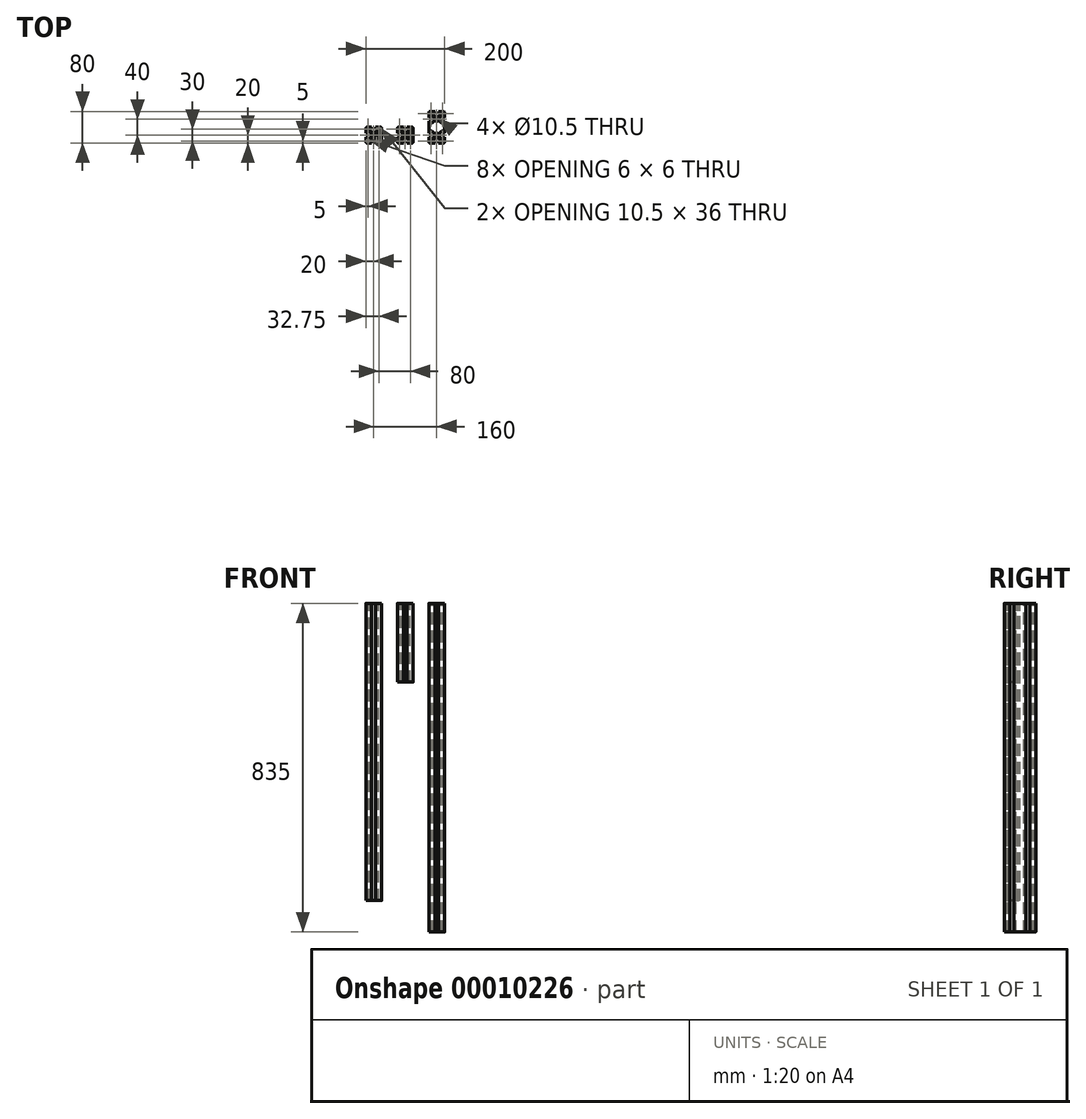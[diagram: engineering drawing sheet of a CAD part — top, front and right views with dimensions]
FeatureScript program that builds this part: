
annotation { "Feature Type Name" : "Feature", "Feature Type Description" : "" }
export const myFeature = defineFeature(function(context is Context, id is Id, definition is map)
    precondition{}
    {
        {
            var Q0;
            Q0=qCreatedBy(makeId("Top.planeOp"),FACE);
            var sketch = newSketch(context, id + "F0", { "sketchPlane" : qUnion([Q0])});
            skLineSegment(sketch, "E0.bottom", {"start": v(97, 20) * mm, "end": v(63, 20) * mm});
            skLineSegment(sketch, "E0.top", {"start": v(97, -20) * mm, "end": v(63, -20) * mm});
            skLineSegment(sketch, "E0.left", {"start": v(100, 17) * mm, "end": v(100, -17) * mm});
            skLineSegment(sketch, "E0.right", {"start": v(60, 17) * mm, "end": v(60, -17) * mm});
            skPoint(sketch, "E1", {"position": v(80, -20) * mm});
            skPoint(sketch, "E2", {"position": v(100, 0) * mm});
            skCircle(sketch, "E3", {"center": v(80, 0) * mm, "radius": 5.25 * mm});
            skPoint(sketch, "E4.visualSharp", {"position": v(100, 20) * mm});
            skArc(sketch, "E4.filletArc", {"start": v(100, 17) * mm, "mid": v(99.12, 19.12) * mm, "end": v(97, 20) * mm});
            skPoint(sketch, "E5.visualSharp", {"position": v(60, 20) * mm});
            skArc(sketch, "E5.filletArc", {"start": v(63, 20) * mm, "mid": v(60.88, 19.12) * mm, "end": v(60, 17) * mm});
            skPoint(sketch, "E6.visualSharp", {"position": v(60, -20) * mm});
            skArc(sketch, "E6.filletArc", {"start": v(60, -17) * mm, "mid": v(60.88, -19.12) * mm, "end": v(63, -20) * mm});
            skPoint(sketch, "E7.visualSharp", {"position": v(100, -20) * mm});
            skArc(sketch, "E7.filletArc", {"start": v(97, -20) * mm, "mid": v(99.12, -19.12) * mm, "end": v(100, -17) * mm});
            skLineSegment(sketch, "E8", {"start": v(85, 20) * mm, "end": v(85, 14.5) * mm});
            skLineSegment(sketch, "E9", {"start": v(85, 14.5) * mm, "end": v(90, 14.5) * mm});
            skLineSegment(sketch, "E10", {"start": v(90, 14.5) * mm, "end": v(90, 12.5) * mm});
            skLineSegment(sketch, "E11", {"start": v(90, 12.5) * mm, "end": v(85, 7.5) * mm});
            skLineSegment(sketch, "E12", {"start": v(85, 7.5) * mm, "end": v(75, 7.5) * mm});
            skLineSegment(sketch, "E13", {"start": v(75, 7.5) * mm, "end": v(70, 12.5) * mm});
            skLineSegment(sketch, "E14", {"start": v(70, 12.5) * mm, "end": v(70, 14.5) * mm});
            skLineSegment(sketch, "E15", {"start": v(70, 14.5) * mm, "end": v(75, 14.5) * mm});
            skLineSegment(sketch, "E16", {"start": v(75, 14.5) * mm, "end": v(75, 20) * mm});
            skPoint(sketch, "E17", {"position": v(80, 7.5) * mm});
            skLineSegment(sketch, "E18.bottom", {"start": v(67, 12) * mm, "end": v(63, 12) * mm});
            skLineSegment(sketch, "E18.top", {"start": v(67, 18) * mm, "end": v(63, 18) * mm});
            skLineSegment(sketch, "E18.left", {"start": v(68, 13) * mm, "end": v(68, 17) * mm});
            skLineSegment(sketch, "E18.right", {"start": v(62, 13) * mm, "end": v(62, 17) * mm});
            skPoint(sketch, "E19.visualSharp", {"position": v(62, 18) * mm});
            skArc(sketch, "E19.filletArc", {"start": v(63, 18) * mm, "mid": v(62.3, 17.7) * mm, "end": v(62, 17) * mm});
            skPoint(sketch, "E20.visualSharp", {"position": v(62, 12) * mm});
            skArc(sketch, "E20.filletArc", {"start": v(62, 13) * mm, "mid": v(62.3, 12.3) * mm, "end": v(63, 12) * mm});
            skPoint(sketch, "E21.visualSharp", {"position": v(68, 12) * mm});
            skArc(sketch, "E21.filletArc", {"start": v(67, 12) * mm, "mid": v(67.7, 12.3) * mm, "end": v(68, 13) * mm});
            skPoint(sketch, "E22.visualSharp", {"position": v(68, 18) * mm});
            skArc(sketch, "E22.filletArc", {"start": v(68, 17) * mm, "mid": v(67.7, 17.7) * mm, "end": v(67, 18) * mm});
            skLineSegment(sketch, "E23.1.0", {"start": v(60, 5) * mm, "end": v(65.5, 5) * mm});
            skLineSegment(sketch, "E23.1.1", {"start": v(65.5, 5) * mm, "end": v(65.5, 10) * mm});
            skLineSegment(sketch, "E23.1.2", {"start": v(65.5, 10) * mm, "end": v(67.5, 10) * mm});
            skLineSegment(sketch, "E23.1.3", {"start": v(67.5, 10) * mm, "end": v(72.5, 5) * mm});
            skLineSegment(sketch, "E23.1.4", {"start": v(72.5, 5) * mm, "end": v(72.5, -5) * mm});
            skLineSegment(sketch, "E23.1.5", {"start": v(72.5, -5) * mm, "end": v(67.5, -10) * mm});
            skLineSegment(sketch, "E23.1.6", {"start": v(67.5, -10) * mm, "end": v(65.5, -10) * mm});
            skLineSegment(sketch, "E23.1.7", {"start": v(65.5, -10) * mm, "end": v(65.5, -5) * mm});
            skLineSegment(sketch, "E23.1.8", {"start": v(65.5, -5) * mm, "end": v(60, -5) * mm});
            skLineSegment(sketch, "E23.1.9", {"start": v(67, -12) * mm, "end": v(63, -12) * mm});
            skArc(sketch, "E23.1.10", {"start": v(63, -12) * mm, "mid": v(62.3, -12.3) * mm, "end": v(62, -13) * mm});
            skLineSegment(sketch, "E23.1.11", {"start": v(62, -13) * mm, "end": v(62, -17) * mm});
            skArc(sketch, "E23.1.12", {"start": v(62, -17) * mm, "mid": v(62.3, -17.7) * mm, "end": v(63, -18) * mm});
            skLineSegment(sketch, "E23.1.13", {"start": v(67, -18) * mm, "end": v(63, -18) * mm});
            skArc(sketch, "E23.1.14", {"start": v(67, -18) * mm, "mid": v(67.7, -17.7) * mm, "end": v(68, -17) * mm});
            skLineSegment(sketch, "E23.1.15", {"start": v(68, -13) * mm, "end": v(68, -17) * mm});
            skArc(sketch, "E23.1.16", {"start": v(68, -13) * mm, "mid": v(67.7, -12.3) * mm, "end": v(67, -12) * mm});
            skLineSegment(sketch, "E23.2.0", {"start": v(75, -20) * mm, "end": v(75, -14.5) * mm});
            skLineSegment(sketch, "E23.2.1", {"start": v(75, -14.5) * mm, "end": v(70, -14.5) * mm});
            skLineSegment(sketch, "E23.2.2", {"start": v(70, -14.5) * mm, "end": v(70, -12.5) * mm});
            skLineSegment(sketch, "E23.2.3", {"start": v(70, -12.5) * mm, "end": v(75, -7.5) * mm});
            skLineSegment(sketch, "E23.2.4", {"start": v(75, -7.5) * mm, "end": v(85, -7.5) * mm});
            skLineSegment(sketch, "E23.2.5", {"start": v(85, -7.5) * mm, "end": v(90, -12.5) * mm});
            skLineSegment(sketch, "E23.2.6", {"start": v(90, -12.5) * mm, "end": v(90, -14.5) * mm});
            skLineSegment(sketch, "E23.2.7", {"start": v(90, -14.5) * mm, "end": v(85, -14.5) * mm});
            skLineSegment(sketch, "E23.2.8", {"start": v(85, -14.5) * mm, "end": v(85, -20) * mm});
            skArc(sketch, "E24.1", {"start": v(97, -18) * mm, "mid": v(97.7, -17.7) * mm, "end": v(98, -17) * mm});
            skArc(sketch, "E24.5", {"start": v(98, 17) * mm, "mid": v(97.7, 17.7) * mm, "end": v(97, 18) * mm});
            skLineSegment(sketch, "E25", {"start": v(97, -18) * mm, "end": v(93, -18) * mm});
            skLineSegment(sketch, "E26", {"start": v(92, -17) * mm, "end": v(92, -9.5) * mm});
            skLineSegment(sketch, "E27", {"start": v(92, -9.5) * mm, "end": v(87.5, -5) * mm});
            skLineSegment(sketch, "E28", {"start": v(87.5, -5) * mm, "end": v(87.5, 5) * mm});
            skLineSegment(sketch, "E29", {"start": v(87.5, 5) * mm, "end": v(92, 9.5) * mm});
            skLineSegment(sketch, "E30", {"start": v(92, 9.5) * mm, "end": v(92, 17) * mm});
            skLineSegment(sketch, "E31", {"start": v(93, 18) * mm, "end": v(97, 18) * mm});
            skPoint(sketch, "E32", {"position": v(87.5, 0) * mm});
            skPoint(sketch, "E33.visualSharp", {"position": v(92, -18) * mm});
            skArc(sketch, "E33.filletArc", {"start": v(92, -17) * mm, "mid": v(92.3, -17.7) * mm, "end": v(93, -18) * mm});
            skPoint(sketch, "E34.visualSharp", {"position": v(92, 18) * mm});
            skArc(sketch, "E34.filletArc", {"start": v(93, 18) * mm, "mid": v(92.3, 17.7) * mm, "end": v(92, 17) * mm});
            skLineSegment(sketch, "E35", {"start": v(98, -17) * mm, "end": v(98, 17) * mm});
            skSolve(sketch);
        }
        {
            var Q0;
            Q0=makeQuery(id+"F0.imprint","IMPRINT",FACE,{"disambiguationData":[TD([[makeQuery(id+"F0.imprint","IMPRINT",EDGE,{"derivedFrom":sQuery(id+"F0.wireOp",EDGE,"E0.left")}),-1.0]])]});
            extrude(context, id + "F1", {"entities" : qUnion([Q0]), "oppositeDirection" : true, "depth" : 755 * mm});
        }
        {
            var Q0;
            Q0=makeQuery(id+"F1.opExtrude","SWEPT_BODY",BODY,{"disambiguationData":[OSD([sQuery(id+"F0.wireOp",EDGE,"E0.bottom"),sQuery(id+"F0.wireOp",EDGE,"E0.top"),sQuery(id+"F0.wireOp",EDGE,"E0.left"),sQuery(id+"F0.wireOp",EDGE,"E0.right"),sQuery(id+"F0.wireOp",EDGE,"E3"),sQuery(id+"F0.wireOp",EDGE,"E4.filletArc"),sQuery(id+"F0.wireOp",EDGE,"E5.filletArc"),sQuery(id+"F0.wireOp",EDGE,"E6.filletArc"),sQuery(id+"F0.wireOp",EDGE,"E7.filletArc"),sQuery(id+"F0.wireOp",EDGE,"E8"),sQuery(id+"F0.wireOp",EDGE,"E9"),sQuery(id+"F0.wireOp",EDGE,"E10"),sQuery(id+"F0.wireOp",EDGE,"E11"),sQuery(id+"F0.wireOp",EDGE,"E12"),sQuery(id+"F0.wireOp",EDGE,"E13"),sQuery(id+"F0.wireOp",EDGE,"E14"),sQuery(id+"F0.wireOp",EDGE,"E15"),sQuery(id+"F0.wireOp",EDGE,"E16"),sQuery(id+"F0.wireOp",EDGE,"E18.bottom"),sQuery(id+"F0.wireOp",EDGE,"E18.top"),sQuery(id+"F0.wireOp",EDGE,"E18.left"),sQuery(id+"F0.wireOp",EDGE,"E18.right"),sQuery(id+"F0.wireOp",EDGE,"E19.filletArc"),sQuery(id+"F0.wireOp",EDGE,"E20.filletArc"),sQuery(id+"F0.wireOp",EDGE,"E21.filletArc"),sQuery(id+"F0.wireOp",EDGE,"E22.filletArc"),sQuery(id+"F0.wireOp",EDGE,"E23.1.0"),sQuery(id+"F0.wireOp",EDGE,"E23.1.1"),sQuery(id+"F0.wireOp",EDGE,"E23.1.2"),sQuery(id+"F0.wireOp",EDGE,"E23.1.3"),sQuery(id+"F0.wireOp",EDGE,"E23.1.4"),sQuery(id+"F0.wireOp",EDGE,"E23.1.5"),sQuery(id+"F0.wireOp",EDGE,"E23.1.6"),sQuery(id+"F0.wireOp",EDGE,"E23.1.7"),sQuery(id+"F0.wireOp",EDGE,"E23.1.8"),sQuery(id+"F0.wireOp",EDGE,"E23.1.9"),sQuery(id+"F0.wireOp",EDGE,"E23.1.10"),sQuery(id+"F0.wireOp",EDGE,"E23.1.11"),sQuery(id+"F0.wireOp",EDGE,"E23.1.12"),sQuery(id+"F0.wireOp",EDGE,"E23.1.13"),sQuery(id+"F0.wireOp",EDGE,"E23.1.14"),sQuery(id+"F0.wireOp",EDGE,"E23.1.15"),sQuery(id+"F0.wireOp",EDGE,"E23.1.16"),sQuery(id+"F0.wireOp",EDGE,"E23.2.0"),sQuery(id+"F0.wireOp",EDGE,"E23.2.1"),sQuery(id+"F0.wireOp",EDGE,"E23.2.2"),sQuery(id+"F0.wireOp",EDGE,"E23.2.3"),sQuery(id+"F0.wireOp",EDGE,"E23.2.4"),sQuery(id+"F0.wireOp",EDGE,"E23.2.5"),sQuery(id+"F0.wireOp",EDGE,"E23.2.6"),sQuery(id+"F0.wireOp",EDGE,"E23.2.7"),sQuery(id+"F0.wireOp",EDGE,"E23.2.8"),sQuery(id+"F0.wireOp",EDGE,"E24.1"),sQuery(id+"F0.wireOp",EDGE,"E24.5"),sQuery(id+"F0.wireOp",EDGE,"E25"),sQuery(id+"F0.wireOp",EDGE,"E26"),sQuery(id+"F0.wireOp",EDGE,"E27"),sQuery(id+"F0.wireOp",EDGE,"E28"),sQuery(id+"F0.wireOp",EDGE,"E29"),sQuery(id+"F0.wireOp",EDGE,"E30"),sQuery(id+"F0.wireOp",EDGE,"E31"),sQuery(id+"F0.wireOp",EDGE,"E33.filletArc"),sQuery(id+"F0.wireOp",EDGE,"E34.filletArc"),sQuery(id+"F0.wireOp",EDGE,"E35")])]});
            transform(context, id + "F2", {"entities" : qUnion([Q0]), "transformType" : TransformType.TRANSLATION_3D, "dx" : 80 * mm, "dy" : 0 * mm, "dz" : 0 * mm, "makeCopy" : true});
        }
        {
            var Q0;
            Q0=makeQuery(id+"F2.opPattern","COPY",FACE,{"derivedFrom":makeQuery(id+"F1.opExtrude","CAP_FACE",FACE,{"disambiguationData":[OSD([sQuery(id+"F0.wireOp",EDGE,"E0.bottom"),sQuery(id+"F0.wireOp",EDGE,"E0.top"),sQuery(id+"F0.wireOp",EDGE,"E0.left"),sQuery(id+"F0.wireOp",EDGE,"E0.right"),sQuery(id+"F0.wireOp",EDGE,"E3"),sQuery(id+"F0.wireOp",EDGE,"E4.filletArc"),sQuery(id+"F0.wireOp",EDGE,"E5.filletArc"),sQuery(id+"F0.wireOp",EDGE,"E6.filletArc"),sQuery(id+"F0.wireOp",EDGE,"E7.filletArc"),sQuery(id+"F0.wireOp",EDGE,"E8"),sQuery(id+"F0.wireOp",EDGE,"E9"),sQuery(id+"F0.wireOp",EDGE,"E10"),sQuery(id+"F0.wireOp",EDGE,"E11"),sQuery(id+"F0.wireOp",EDGE,"E12"),sQuery(id+"F0.wireOp",EDGE,"E13"),sQuery(id+"F0.wireOp",EDGE,"E14"),sQuery(id+"F0.wireOp",EDGE,"E15"),sQuery(id+"F0.wireOp",EDGE,"E16"),sQuery(id+"F0.wireOp",EDGE,"E18.bottom"),sQuery(id+"F0.wireOp",EDGE,"E18.top"),sQuery(id+"F0.wireOp",EDGE,"E18.left"),sQuery(id+"F0.wireOp",EDGE,"E18.right"),sQuery(id+"F0.wireOp",EDGE,"E19.filletArc"),sQuery(id+"F0.wireOp",EDGE,"E20.filletArc"),sQuery(id+"F0.wireOp",EDGE,"E21.filletArc"),sQuery(id+"F0.wireOp",EDGE,"E22.filletArc"),sQuery(id+"F0.wireOp",EDGE,"E23.1.0"),sQuery(id+"F0.wireOp",EDGE,"E23.1.1"),sQuery(id+"F0.wireOp",EDGE,"E23.1.2"),sQuery(id+"F0.wireOp",EDGE,"E23.1.3"),sQuery(id+"F0.wireOp",EDGE,"E23.1.4"),sQuery(id+"F0.wireOp",EDGE,"E23.1.5"),sQuery(id+"F0.wireOp",EDGE,"E23.1.6"),sQuery(id+"F0.wireOp",EDGE,"E23.1.7"),sQuery(id+"F0.wireOp",EDGE,"E23.1.8"),sQuery(id+"F0.wireOp",EDGE,"E23.1.9"),sQuery(id+"F0.wireOp",EDGE,"E23.1.10"),sQuery(id+"F0.wireOp",EDGE,"E23.1.11"),sQuery(id+"F0.wireOp",EDGE,"E23.1.12"),sQuery(id+"F0.wireOp",EDGE,"E23.1.13"),sQuery(id+"F0.wireOp",EDGE,"E23.1.14"),sQuery(id+"F0.wireOp",EDGE,"E23.1.15"),sQuery(id+"F0.wireOp",EDGE,"E23.1.16"),sQuery(id+"F0.wireOp",EDGE,"E23.2.0"),sQuery(id+"F0.wireOp",EDGE,"E23.2.1"),sQuery(id+"F0.wireOp",EDGE,"E23.2.2"),sQuery(id+"F0.wireOp",EDGE,"E23.2.3"),sQuery(id+"F0.wireOp",EDGE,"E23.2.4"),sQuery(id+"F0.wireOp",EDGE,"E23.2.5"),sQuery(id+"F0.wireOp",EDGE,"E23.2.6"),sQuery(id+"F0.wireOp",EDGE,"E23.2.7"),sQuery(id+"F0.wireOp",EDGE,"E23.2.8"),sQuery(id+"F0.wireOp",EDGE,"E24.1"),sQuery(id+"F0.wireOp",EDGE,"E24.5"),sQuery(id+"F0.wireOp",EDGE,"E25"),sQuery(id+"F0.wireOp",EDGE,"E26"),sQuery(id+"F0.wireOp",EDGE,"E27"),sQuery(id+"F0.wireOp",EDGE,"E28"),sQuery(id+"F0.wireOp",EDGE,"E29"),sQuery(id+"F0.wireOp",EDGE,"E30"),sQuery(id+"F0.wireOp",EDGE,"E31"),sQuery(id+"F0.wireOp",EDGE,"E33.filletArc"),sQuery(id+"F0.wireOp",EDGE,"E34.filletArc"),sQuery(id+"F0.wireOp",EDGE,"E35")])],"isStart":false}),"instanceName":"1"});
            extrude(context, id + "F3", {"entities" : qUnion([Q0]), "operationType" : NewBodyOperationType.REMOVE, "oppositeDirection" : true, "depth" : 555 * mm});
        }
        {
            var Q0;
            Q0=qCreatedBy(makeId("Top.planeOp"),FACE);
            var sketch = newSketch(context, id + "F4", { "sketchPlane" : qUnion([Q0])});
            skLineSegment(sketch, "E36.top", {"start": v(257, -20) * mm, "end": v(223, -20) * mm});
            skLineSegment(sketch, "E36.left", {"start": v(260, 17) * mm, "end": v(260, -17) * mm});
            skLineSegment(sketch, "E36.right", {"start": v(220, 17) * mm, "end": v(220, -17) * mm});
            skPoint(sketch, "E37", {"position": v(240, -20) * mm});
            skPoint(sketch, "E38", {"position": v(260, 0) * mm});
            skCircle(sketch, "E39", {"center": v(240, 0) * mm, "radius": 5.25 * mm});
            skPoint(sketch, "E40.visualSharp", {"position": v(220, -20) * mm});
            skArc(sketch, "E40.filletArc", {"start": v(220, -17) * mm, "mid": v(220.88, -19.12) * mm, "end": v(223, -20) * mm});
            skPoint(sketch, "E41.visualSharp", {"position": v(260, -20) * mm});
            skArc(sketch, "E41.filletArc", {"start": v(257, -20) * mm, "mid": v(259.12, -19.12) * mm, "end": v(260, -17) * mm});
            skLineSegment(sketch, "E42.1.9", {"start": v(227, -12) * mm, "end": v(223, -12) * mm});
            skArc(sketch, "E42.1.10", {"start": v(223, -12) * mm, "mid": v(222.3, -12.3) * mm, "end": v(222, -13) * mm});
            skLineSegment(sketch, "E42.1.11", {"start": v(222, -13) * mm, "end": v(222, -17) * mm});
            skArc(sketch, "E42.1.12", {"start": v(222, -17) * mm, "mid": v(222.3, -17.7) * mm, "end": v(223, -18) * mm});
            skLineSegment(sketch, "E42.1.13", {"start": v(227, -18) * mm, "end": v(223, -18) * mm});
            skArc(sketch, "E42.1.14", {"start": v(227, -18) * mm, "mid": v(227.7, -17.7) * mm, "end": v(228, -17) * mm});
            skLineSegment(sketch, "E42.1.15", {"start": v(228, -13) * mm, "end": v(228, -17) * mm});
            skArc(sketch, "E42.1.16", {"start": v(228, -13) * mm, "mid": v(227.7, -12.3) * mm, "end": v(227, -12) * mm});
            skLineSegment(sketch, "E42.2.0", {"start": v(235, -20) * mm, "end": v(235, -14.5) * mm});
            skLineSegment(sketch, "E42.2.1", {"start": v(235, -14.5) * mm, "end": v(230, -14.5) * mm});
            skLineSegment(sketch, "E42.2.2", {"start": v(230, -14.5) * mm, "end": v(230, -12.5) * mm});
            skLineSegment(sketch, "E42.2.3", {"start": v(230, -12.5) * mm, "end": v(235, -7.5) * mm});
            skLineSegment(sketch, "E42.2.4", {"start": v(235, -7.5) * mm, "end": v(245, -7.5) * mm});
            skLineSegment(sketch, "E42.2.5", {"start": v(245, -7.5) * mm, "end": v(250, -12.5) * mm});
            skLineSegment(sketch, "E42.2.6", {"start": v(250, -12.5) * mm, "end": v(250, -14.5) * mm});
            skLineSegment(sketch, "E42.2.7", {"start": v(250, -14.5) * mm, "end": v(245, -14.5) * mm});
            skLineSegment(sketch, "E42.2.8", {"start": v(245, -14.5) * mm, "end": v(245, -20) * mm});
            skLineSegment(sketch, "E43.1.0", {"start": v(247.5, 5) * mm, "end": v(252.5, 10) * mm});
            skLineSegment(sketch, "E43.1.2", {"start": v(253, -18) * mm, "end": v(257, -18) * mm});
            skLineSegment(sketch, "E43.1.3", {"start": v(252.5, -10) * mm, "end": v(247.5, -5) * mm});
            skLineSegment(sketch, "E43.1.4", {"start": v(258, -13) * mm, "end": v(258, -17) * mm});
            skLineSegment(sketch, "E43.1.5", {"start": v(252, -13) * mm, "end": v(252, -17) * mm});
            skLineSegment(sketch, "E43.1.6", {"start": v(254.5, -5) * mm, "end": v(254.5, -10) * mm});
            skLineSegment(sketch, "E43.1.7", {"start": v(260, -5) * mm, "end": v(254.5, -5) * mm});
            skLineSegment(sketch, "E43.1.8", {"start": v(247.5, -5) * mm, "end": v(247.5, 5) * mm});
            skLineSegment(sketch, "E43.1.9", {"start": v(254.5, 5) * mm, "end": v(260, 5) * mm});
            skLineSegment(sketch, "E43.1.10", {"start": v(253, -12) * mm, "end": v(257, -12) * mm});
            skLineSegment(sketch, "E43.1.11", {"start": v(254.5, 10) * mm, "end": v(254.5, 5) * mm});
            skLineSegment(sketch, "E43.1.13", {"start": v(254.5, -10) * mm, "end": v(252.5, -10) * mm});
            skArc(sketch, "E43.1.14", {"start": v(252, -17) * mm, "mid": v(252.3, -17.7) * mm, "end": v(253, -18) * mm});
            skLineSegment(sketch, "E43.1.15", {"start": v(252.5, 10) * mm, "end": v(254.5, 10) * mm});
            skArc(sketch, "E43.1.16", {"start": v(257, -18) * mm, "mid": v(257.7, -17.7) * mm, "end": v(258, -17) * mm});
            skArc(sketch, "E43.1.17", {"start": v(258, -13) * mm, "mid": v(257.7, -12.3) * mm, "end": v(257, -12) * mm});
            skArc(sketch, "E43.1.18", {"start": v(253, -12) * mm, "mid": v(252.3, -12.3) * mm, "end": v(252, -13) * mm});
            skLineSegment(sketch, "E43.3.0", {"start": v(232.5, -5) * mm, "end": v(227.5, -10) * mm});
            skPoint(sketch, "E43.3.1", {"position": v(220, 0) * mm});
            skLineSegment(sketch, "E43.3.3", {"start": v(227.5, 10) * mm, "end": v(232.5, 5) * mm});
            skLineSegment(sketch, "E43.3.6", {"start": v(225.5, 5) * mm, "end": v(225.5, 10) * mm});
            skLineSegment(sketch, "E43.3.7", {"start": v(220, 5) * mm, "end": v(225.5, 5) * mm});
            skLineSegment(sketch, "E43.3.8", {"start": v(232.5, 5) * mm, "end": v(232.5, -5) * mm});
            skLineSegment(sketch, "E43.3.9", {"start": v(225.5, -5) * mm, "end": v(220, -5) * mm});
            skLineSegment(sketch, "E43.3.11", {"start": v(225.5, -10) * mm, "end": v(225.5, -5) * mm});
            skLineSegment(sketch, "E43.3.13", {"start": v(225.5, 10) * mm, "end": v(227.5, 10) * mm});
            skLineSegment(sketch, "E43.3.15", {"start": v(227.5, -10) * mm, "end": v(225.5, -10) * mm});
            skPoint(sketch, "E44.0.MirrorP", {"position": v(240, 40) * mm});
            skPoint(sketch, "E44.1.MirrorP", {"position": v(240, 40) * mm});
            skPoint(sketch, "E44.4.MirrorP", {"position": v(240, 40) * mm});
            skArc(sketch, "E44.5.MirrorCS", {"start": v(222, 57) * mm, "mid": v(222.3, 57.7) * mm, "end": v(223, 58) * mm});
            skArc(sketch, "E44.6.MirrorCS", {"start": v(257, 58) * mm, "mid": v(257.7, 57.7) * mm, "end": v(258, 57) * mm});
            skLineSegment(sketch, "E44.8.MirrorCS", {"start": v(227.5, 50) * mm, "end": v(225.5, 50) * mm});
            skLineSegment(sketch, "E44.9.MirrorCS", {"start": v(250, 52.5) * mm, "end": v(250, 54.5) * mm});
            skPoint(sketch, "E44.10.MirrorP", {"position": v(240, 40) * mm});
            skLineSegment(sketch, "E44.12.MirrorCS", {"start": v(252.5, 30) * mm, "end": v(254.5, 30) * mm});
            skArc(sketch, "E44.13.MirrorCS", {"start": v(253, 52) * mm, "mid": v(252.3, 52.3) * mm, "end": v(252, 53) * mm});
            skLineSegment(sketch, "E44.15.MirrorCS", {"start": v(254.5, 50) * mm, "end": v(252.5, 50) * mm});
            skLineSegment(sketch, "E44.16.MirrorCS", {"start": v(225.5, 30) * mm, "end": v(227.5, 30) * mm});
            skArc(sketch, "E44.17.MirrorCS", {"start": v(257, 60) * mm, "mid": v(259.12, 59.12) * mm, "end": v(260, 57) * mm});
            skLineSegment(sketch, "E44.19.MirrorCS", {"start": v(230, 54.5) * mm, "end": v(230, 52.5) * mm});
            skArc(sketch, "E44.20.MirrorCS", {"start": v(220, 57) * mm, "mid": v(220.88, 59.12) * mm, "end": v(223, 60) * mm});
            skArc(sketch, "E44.23.MirrorCS", {"start": v(228, 53) * mm, "mid": v(227.7, 52.3) * mm, "end": v(227, 52) * mm});
            skArc(sketch, "E44.24.MirrorCS", {"start": v(223, 52) * mm, "mid": v(222.3, 52.3) * mm, "end": v(222, 53) * mm});
            skArc(sketch, "E44.25.MirrorCS", {"start": v(258, 53) * mm, "mid": v(257.7, 52.3) * mm, "end": v(257, 52) * mm});
            skArc(sketch, "E44.29.MirrorCS", {"start": v(252, 57) * mm, "mid": v(252.3, 57.7) * mm, "end": v(253, 58) * mm});
            skArc(sketch, "E44.31.MirrorCS", {"start": v(227, 58) * mm, "mid": v(227.7, 57.7) * mm, "end": v(228, 57) * mm});
            skLineSegment(sketch, "E44.32.MirrorCS", {"start": v(225.5, 35) * mm, "end": v(225.5, 30) * mm});
            skLineSegment(sketch, "E44.34.MirrorCS", {"start": v(247.5, 45) * mm, "end": v(247.5, 35) * mm});
            skLineSegment(sketch, "E44.35.MirrorCS", {"start": v(235, 60) * mm, "end": v(235, 54.5) * mm});
            skLineSegment(sketch, "E44.38.MirrorCS", {"start": v(258, 53) * mm, "end": v(258, 57) * mm});
            skPoint(sketch, "E44.39.MirrorP", {"position": v(260, 60) * mm});
            skLineSegment(sketch, "E44.40.MirrorCS", {"start": v(260, 45) * mm, "end": v(254.5, 45) * mm});
            skLineSegment(sketch, "E44.41.MirrorCS", {"start": v(247.5, 35) * mm, "end": v(252.5, 30) * mm});
            skLineSegment(sketch, "E44.42.MirrorCS", {"start": v(254.5, 45) * mm, "end": v(254.5, 50) * mm});
            skLineSegment(sketch, "E44.43.MirrorCS", {"start": v(225.5, 45) * mm, "end": v(220, 45) * mm});
            skLineSegment(sketch, "E44.44.MirrorCS", {"start": v(254.5, 30) * mm, "end": v(254.5, 35) * mm});
            skLineSegment(sketch, "E44.46.MirrorCS", {"start": v(230, 52.5) * mm, "end": v(235, 47.5) * mm});
            skLineSegment(sketch, "E44.47.MirrorCS", {"start": v(245, 47.5) * mm, "end": v(250, 52.5) * mm});
            skLineSegment(sketch, "E44.48.MirrorCS", {"start": v(227.5, 30) * mm, "end": v(232.5, 35) * mm});
            skLineSegment(sketch, "E44.49.MirrorCS", {"start": v(232.5, 35) * mm, "end": v(232.5, 45) * mm});
            skPoint(sketch, "E44.50.MirrorP", {"position": v(220, 20) * mm});
            skPoint(sketch, "E44.51.MirrorP", {"position": v(220, 40) * mm});
            skLineSegment(sketch, "E44.52.MirrorCS", {"start": v(250, 54.5) * mm, "end": v(245, 54.5) * mm});
            skCircle(sketch, "E44.53.MirrorC", {"center": v(240, 40) * mm, "radius": 5.25 * mm});
            skLineSegment(sketch, "E44.57.MirrorCS", {"start": v(254.5, 35) * mm, "end": v(260, 35) * mm});
            skPoint(sketch, "E44.58.MirrorP", {"position": v(240, 40) * mm});
            skLineSegment(sketch, "E44.60.MirrorCS", {"start": v(225.5, 50) * mm, "end": v(225.5, 45) * mm});
            skLineSegment(sketch, "E44.61.MirrorCS", {"start": v(235, 47.5) * mm, "end": v(245, 47.5) * mm});
            skLineSegment(sketch, "E44.62.MirrorCS", {"start": v(227, 52) * mm, "end": v(223, 52) * mm});
            skLineSegment(sketch, "E44.63.MirrorCS", {"start": v(253, 58) * mm, "end": v(257, 58) * mm});
            skLineSegment(sketch, "E44.64.MirrorCS", {"start": v(227, 58) * mm, "end": v(223, 58) * mm});
            skLineSegment(sketch, "E44.65.MirrorCS", {"start": v(257, 60) * mm, "end": v(223, 60) * mm});
            skLineSegment(sketch, "E44.66.MirrorCS", {"start": v(232.5, 45) * mm, "end": v(227.5, 50) * mm});
            skLineSegment(sketch, "E44.68.MirrorCS", {"start": v(252, 53) * mm, "end": v(252, 57) * mm});
            skPoint(sketch, "E44.69.MirrorP", {"position": v(220, 60) * mm});
            skLineSegment(sketch, "E44.70.MirrorCS", {"start": v(220, 23) * mm, "end": v(220, 57) * mm});
            skPoint(sketch, "E44.73.MirrorP", {"position": v(260, 20) * mm});
            skPoint(sketch, "E44.74.MirrorP", {"position": v(240, 20) * mm});
            skPoint(sketch, "E44.76.MirrorP", {"position": v(260, 40) * mm});
            skLineSegment(sketch, "E44.78.MirrorCS", {"start": v(228, 53) * mm, "end": v(228, 57) * mm});
            skLineSegment(sketch, "E44.80.MirrorCS", {"start": v(245, 54.5) * mm, "end": v(245, 60) * mm});
            skLineSegment(sketch, "E44.81.MirrorCS", {"start": v(235, 54.5) * mm, "end": v(230, 54.5) * mm});
            skPoint(sketch, "E44.82.MirrorP", {"position": v(240, 60) * mm});
            skLineSegment(sketch, "E44.85.MirrorCS", {"start": v(253, 52) * mm, "end": v(257, 52) * mm});
            skLineSegment(sketch, "E44.86.MirrorCS", {"start": v(222, 53) * mm, "end": v(222, 57) * mm});
            skPoint(sketch, "E44.87.MirrorP", {"position": v(260, 60) * mm});
            skLineSegment(sketch, "E44.88.MirrorCS", {"start": v(252.5, 50) * mm, "end": v(247.5, 45) * mm});
            skLineSegment(sketch, "E44.89.MirrorCS", {"start": v(220, 35) * mm, "end": v(225.5, 35) * mm});
            skPoint(sketch, "E44.90.MirrorP", {"position": v(260, 40) * mm});
            skLineSegment(sketch, "E44.91.MirrorCS", {"start": v(260, 23) * mm, "end": v(260, 57) * mm});
            skLineSegment(sketch, "E45", {"start": v(220, 23) * mm, "end": v(220, 17) * mm});
            skLineSegment(sketch, "E46", {"start": v(260, 23) * mm, "end": v(260, 17) * mm});
            skSolve(sketch);
        }
        {
            var Q0;
            Q0=makeQuery(id+"F4.imprint","IMPRINT",FACE,{"disambiguationData":[TD([[makeQuery(id+"F4.imprint","IMPRINT",EDGE,{"derivedFrom":sQuery(id+"F4.wireOp",EDGE,"E39")}),-1.0]])]});
            extrude(context, id + "F5", {"entities" : qUnion([Q0]), "oppositeDirection" : true, "depth" : 835 * mm});
        }
    });
